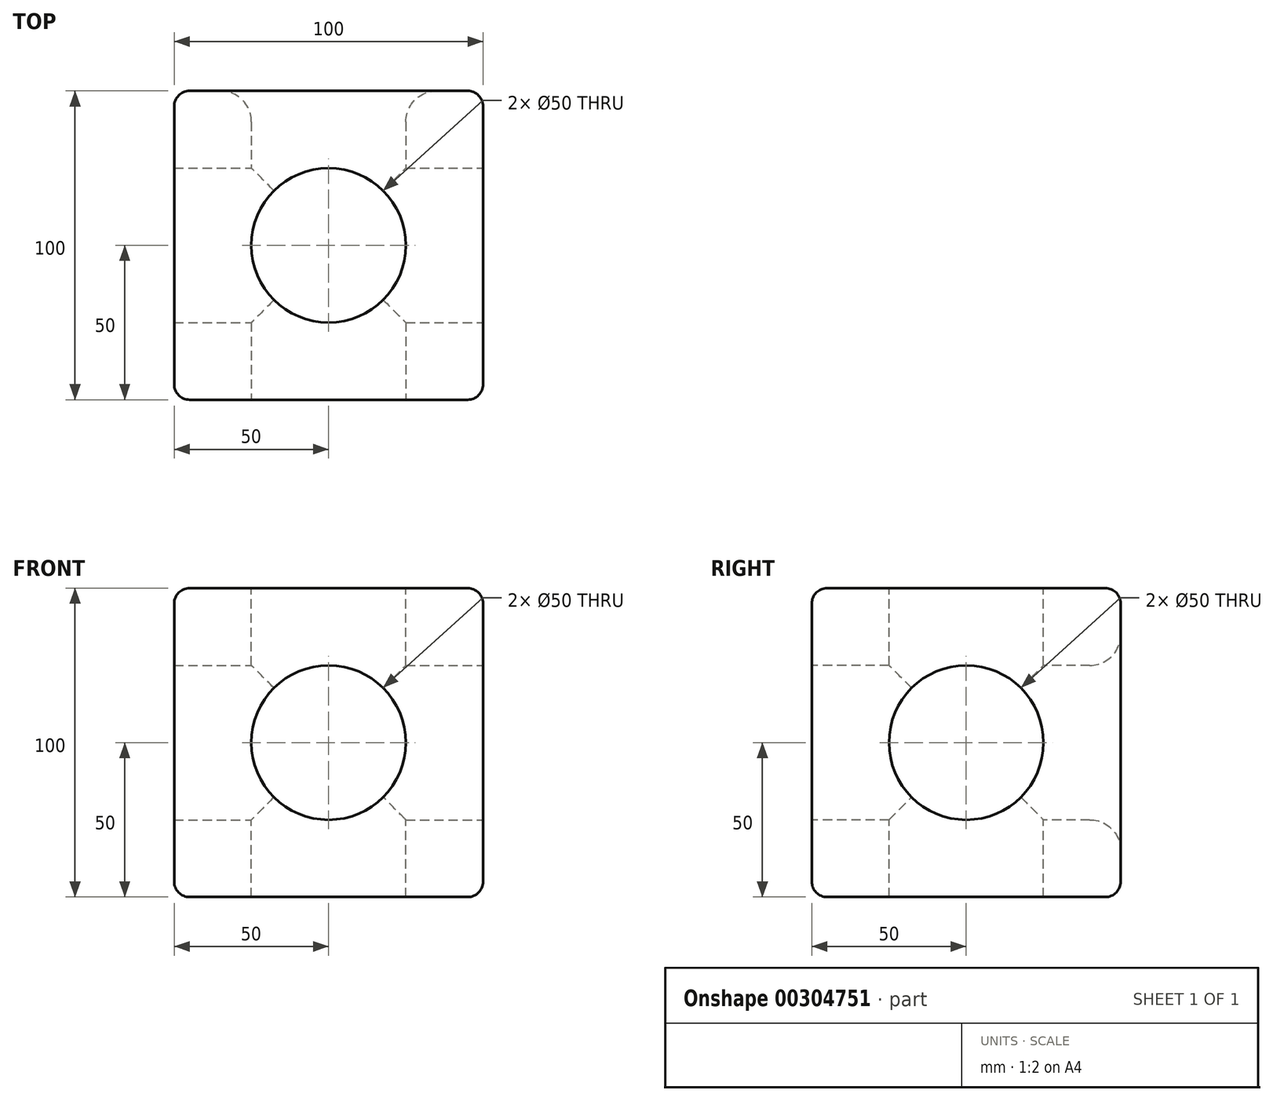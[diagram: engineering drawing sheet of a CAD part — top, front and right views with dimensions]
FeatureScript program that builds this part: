
annotation { "Feature Type Name" : "Feature", "Feature Type Description" : "" }
export const myFeature = defineFeature(function(context is Context, id is Id, definition is map)
    precondition{}
    {
        {
            var Q0;
            Q0=qCreatedBy(makeId("Front.planeOp"),FACE);
            var sketch = newSketch(context, id + "F0", { "sketchPlane" : qUnion([Q0])});
            skLineSegment(sketch, "E0.bottom", {"start": v(50, -50) * mm, "end": v(-50, -50) * mm});
            skLineSegment(sketch, "E0.top", {"start": v(50, 50) * mm, "end": v(-50, 50) * mm});
            skLineSegment(sketch, "E0.left", {"start": v(50, -50) * mm, "end": v(50, 50) * mm});
            skLineSegment(sketch, "E0.right", {"start": v(-50, -50) * mm, "end": v(-50, 50) * mm});
            skPoint(sketch, "E0.middle", {"position": v(0, 0) * mm});
            skSolve(sketch);
        }
        {
            var Q0;
            Q0=makeQuery(id+"F0.imprint","IMPRINT",FACE,{"disambiguationData":[TD([[makeQuery(id+"F0.imprint","IMPRINT",EDGE,{"derivedFrom":sQuery(id+"F0.wireOp",EDGE,"E0.bottom")}),-1.0]])]});
            extrude(context, id + "F1", {"entities" : qUnion([Q0]), "endBound" : BoundingType.SYMMETRIC, "depth" : 100 * mm});
        }
        {
            var Q0;
            Q0=makeQuery(id+"F1.opExtrude","CAP_FACE",FACE,{"disambiguationData":[OSD([sQuery(id+"F0.wireOp",EDGE,"E0.bottom"),sQuery(id+"F0.wireOp",EDGE,"E0.top"),sQuery(id+"F0.wireOp",EDGE,"E0.left"),sQuery(id+"F0.wireOp",EDGE,"E0.right")])],"isStart":false});
            var sketch = newSketch(context, id + "F2", { "sketchPlane" : qUnion([Q0])});
            skCircle(sketch, "E1", {"center": v(0, 0) * mm, "radius": 25 * mm});
            skSolve(sketch);
        }
        {
            var Q0;
            Q0=makeQuery(id+"F2.imprint","IMPRINT",FACE,{"disambiguationData":[TD([[makeQuery(id+"F2.imprint","IMPRINT",EDGE,{"derivedFrom":sQuery(id+"F2.wireOp",EDGE,"E1")}),1.0]])]});
            extrude(context, id + "F3", {"entities" : qUnion([Q0]), "operationType" : NewBodyOperationType.REMOVE, "oppositeDirection" : true, "depth" : 157 * mm});
        }
        {
            var Q0;
            Q0=makeQuery(id+"F1.opExtrude","SWEPT_FACE",FACE,{"disambiguationData":[OSD([sQuery(id+"F0.wireOp",EDGE,"E0.left")])]});
            var sketch = newSketch(context, id + "F4", { "sketchPlane" : qUnion([Q0])});
            skCircle(sketch, "E2", {"center": v(0, 0) * mm, "radius": 25 * mm});
            skSolve(sketch);
        }
        {
            var Q0;
            Q0 = qSketchRegion(id + "F4", true);
            extrude(context, id + "F5", {"entities" : qUnion([Q0]), "operationType" : NewBodyOperationType.REMOVE, "oppositeDirection" : true, "depth" : 100 * mm});
        }
        {
            var Q0;
            Q0=makeQuery(id+"F1.opExtrude","SWEPT_FACE",FACE,{"disambiguationData":[OSD([sQuery(id+"F0.wireOp",EDGE,"E0.top")])]});
            var sketch = newSketch(context, id + "F6", { "sketchPlane" : qUnion([Q0])});
            skCircle(sketch, "E3", {"center": v(0, 0) * mm, "radius": 25 * mm});
            skSolve(sketch);
        }
        {
            var Q0;
            Q0=makeQuery(id+"F6.imprint","IMPRINT",FACE,{"disambiguationData":[TD([[makeQuery(id+"F6.imprint","IMPRINT",EDGE,{"derivedFrom":sQuery(id+"F6.wireOp",EDGE,"E3")}),1.0]])]});
            extrude(context, id + "F7", {"entities" : qUnion([Q0]), "operationType" : NewBodyOperationType.REMOVE, "oppositeDirection" : true, "depth" : 100 * mm});
        }
        {
            var Q0;
            Q0=makeQuery(id+"F7.boolean.opBoolean","COPY",EDGE,{"derivedFrom":makeQuery(id+"F7.opExtrude","CAP_EDGE",EDGE,{"disambiguationData":[OSD([sQuery(id+"F6.wireOp",EDGE,"E3")])],"isStart":true})});
            var Q1;
            Q1=makeQuery(id+"F5.boolean.opBoolean","COPY",EDGE,{"derivedFrom":makeQuery(id+"F5.opExtrude","CAP_EDGE",EDGE,{"disambiguationData":[OSD([sQuery(id+"F4.wireOp",EDGE,"E2")])],"isStart":true})});
            var Q2;
            Q2=makeQuery(id+"F3.boolean.opBoolean","INTERSECT",EDGE,{"derivedFrom":[makeQuery(id+"F1.opExtrude","CAP_FACE",FACE,{"disambiguationData":[OSD([sQuery(id+"F0.wireOp",EDGE,"E0.bottom"),sQuery(id+"F0.wireOp",EDGE,"E0.top"),sQuery(id+"F0.wireOp",EDGE,"E0.left"),sQuery(id+"F0.wireOp",EDGE,"E0.right")])],"isStart":true}),makeQuery(id+"F3.opExtrude","SWEPT_FACE",FACE,{"disambiguationData":[OSD([sQuery(id+"F2.wireOp",EDGE,"E1")])]})]});
            var Q3;
            Q3=makeQuery(id+"F7.boolean.opBoolean","COPY",EDGE,{"derivedFrom":makeQuery(id+"F7.opExtrude","CAP_EDGE",EDGE,{"disambiguationData":[OSD([sQuery(id+"F6.wireOp",EDGE,"E3")])],"isStart":false})});
            var Q4;
            Q4=makeQuery(id+"F3.boolean.opBoolean","COPY",EDGE,{"derivedFrom":makeQuery(id+"F3.opExtrude","CAP_EDGE",EDGE,{"disambiguationData":[OSD([sQuery(id+"F2.wireOp",EDGE,"E1")])],"isStart":true})});
            var Q5;
            Q5=makeQuery(id+"F5.boolean.opBoolean","COPY",EDGE,{"derivedFrom":makeQuery(id+"F5.opExtrude","CAP_EDGE",EDGE,{"disambiguationData":[OSD([sQuery(id+"F4.wireOp",EDGE,"E2")])],"isStart":false})});
            fillet(context, id + "F8", {"entities" : qUnion([Q0, Q1, Q2, Q3, Q4, Q5]), "radius" : 10 * mm, "tangentPropagation" : true, "allowEdgeOverflow" : false});
        }
        {
            var Q0;
            Q0=makeQuery(id+"F1.opExtrude","CAP_EDGE",EDGE,{"disambiguationData":[OSD([sQuery(id+"F0.wireOp",EDGE,"E0.top")])],"isStart":true});
            var Q1;
            Q1=makeQuery(id+"F1.opExtrude","SWEPT_EDGE",EDGE,{"disambiguationData":[OSD([sQuery(id+"F0.wireOp",EDGE,"E0.top"),sQuery(id+"F0.wireOp",EDGE,"E0.left")])]});
            var Q2;
            Q2=makeQuery(id+"F1.opExtrude","CAP_EDGE",EDGE,{"disambiguationData":[OSD([sQuery(id+"F0.wireOp",EDGE,"E0.left")])],"isStart":true});
            var Q3;
            Q3=makeQuery(id+"F1.opExtrude","SWEPT_EDGE",EDGE,{"disambiguationData":[OSD([sQuery(id+"F0.wireOp",EDGE,"E0.top"),sQuery(id+"F0.wireOp",EDGE,"E0.right")])]});
            var Q4;
            Q4=makeQuery(id+"F1.opExtrude","CAP_EDGE",EDGE,{"disambiguationData":[OSD([sQuery(id+"F0.wireOp",EDGE,"E0.right")])],"isStart":true});
            var Q5;
            Q5=makeQuery(id+"F1.opExtrude","CAP_EDGE",EDGE,{"disambiguationData":[OSD([sQuery(id+"F0.wireOp",EDGE,"E0.bottom")])],"isStart":true});
            var Q6;
            Q6=makeQuery(id+"F1.opExtrude","SWEPT_EDGE",EDGE,{"disambiguationData":[OSD([sQuery(id+"F0.wireOp",EDGE,"E0.bottom"),sQuery(id+"F0.wireOp",EDGE,"E0.right")])]});
            var Q7;
            Q7=makeQuery(id+"F1.opExtrude","CAP_EDGE",EDGE,{"disambiguationData":[OSD([sQuery(id+"F0.wireOp",EDGE,"E0.right")])],"isStart":false});
            var Q8;
            Q8=makeQuery(id+"F1.opExtrude","CAP_EDGE",EDGE,{"disambiguationData":[OSD([sQuery(id+"F0.wireOp",EDGE,"E0.top")])],"isStart":false});
            var Q9;
            Q9=makeQuery(id+"F1.opExtrude","SWEPT_EDGE",EDGE,{"disambiguationData":[OSD([sQuery(id+"F0.wireOp",EDGE,"E0.bottom"),sQuery(id+"F0.wireOp",EDGE,"E0.left")])]});
            var Q10;
            Q10=makeQuery(id+"F1.opExtrude","CAP_EDGE",EDGE,{"disambiguationData":[OSD([sQuery(id+"F0.wireOp",EDGE,"E0.left")])],"isStart":false});
            var Q11;
            Q11=makeQuery(id+"F1.opExtrude","CAP_EDGE",EDGE,{"disambiguationData":[OSD([sQuery(id+"F0.wireOp",EDGE,"E0.bottom")])],"isStart":false});
            fillet(context, id + "F9", {"entities" : qUnion([Q0, Q1, Q2, Q3, Q4, Q5, Q6, Q7, Q8, Q9, Q10, Q11]), "radius" : 5 * mm, "tangentPropagation" : true, "allowEdgeOverflow" : false});
        }
    });
